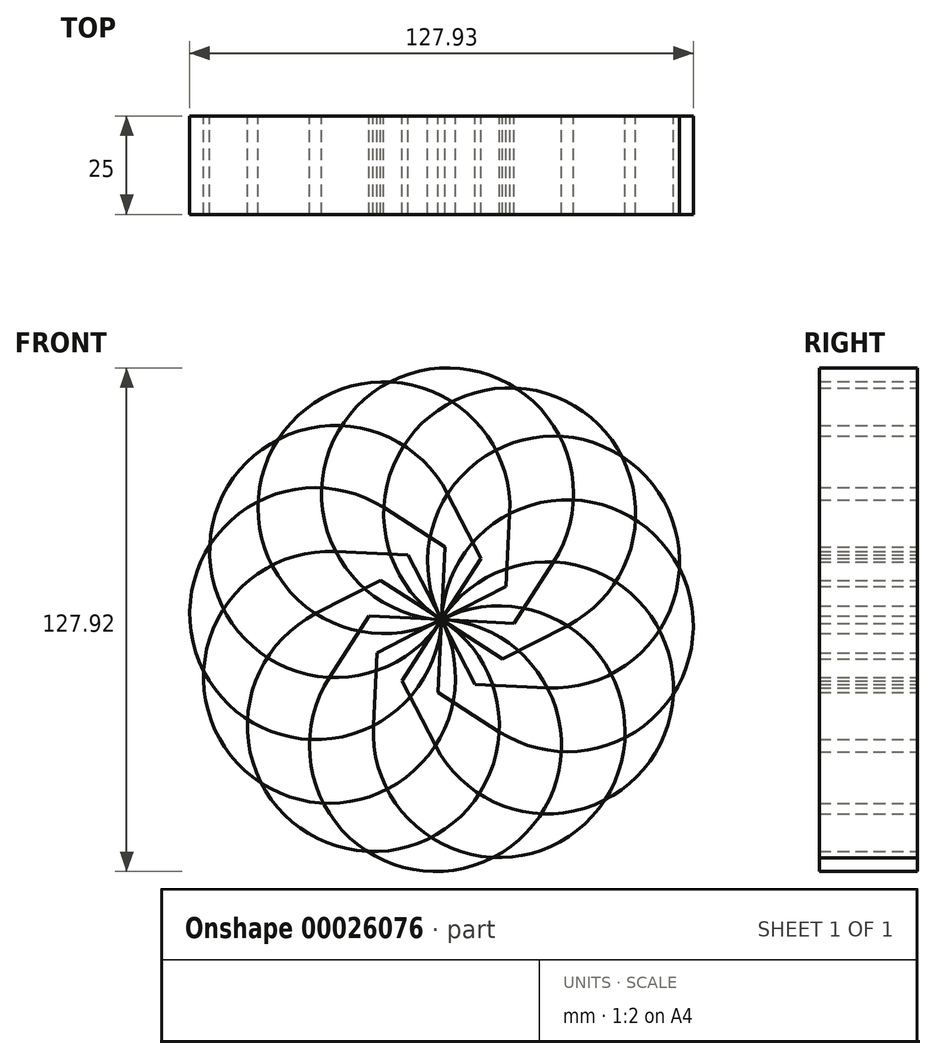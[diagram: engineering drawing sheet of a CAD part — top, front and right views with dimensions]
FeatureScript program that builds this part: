
annotation { "Feature Type Name" : "Feature", "Feature Type Description" : "" }
export const myFeature = defineFeature(function(context is Context, id is Id, definition is map)
    precondition{}
    {
        {
            var Q0;
            Q0=qCreatedBy(makeId("Front.planeOp"),FACE);
            var sketch = newSketch(context, id + "F0", { "sketchPlane" : qUnion([Q0])});
            skLineSegment(sketch, "E0.bottom", {"start": v(32.22, 19.52) * mm, "end": v(50.67, 18.63) * mm});
            skLineSegment(sketch, "E0.right", {"start": v(50.67, 18.63) * mm, "end": v(59.12, 2.2) * mm});
            skArc(sketch, "E1", {"start": v(32.22, 19.52) * mm, "mid": v(13.35, -39.35) * mm, "end": v(59.12, 2.2) * mm});
            skLineSegment(sketch, "E2.0", {"start": v(53.8, 23.48) * mm, "end": v(63, 5.6) * mm});
            skLineSegment(sketch, "E2.1", {"start": v(32.46, 24.52) * mm, "end": v(53.8, 23.48) * mm});
            skSolve(sketch);
        }
        {
            var Q0;
            Q0=makeQuery(id+"F0.imprint","IMPRINT",FACE,{"disambiguationData":[TD([[makeQuery(id+"F0.imprint","IMPRINT",EDGE,{"derivedFrom":sQuery(id+"F0.wireOp",EDGE,"E0.bottom")}),-1.0]])]});
            extrude(context, id + "F1", {"entities" : qUnion([Q0]), "endBound" : BoundingType.SYMMETRIC, "depth" : 25 * mm});
        }
        {
            var Q0;
            Q0=makeQuery(id+"F1.opExtrude","SWEPT_BODY",BODY,{"disambiguationData":[OSD([sQuery(id+"F0.wireOp",EDGE,"E0.bottom"),sQuery(id+"F0.wireOp",EDGE,"E0.right"),sQuery(id+"F0.wireOp",EDGE,"E1")])]});
            var Q1;
            Q1=makeQuery(id+"F1.opExtrude","SWEPT_EDGE",EDGE,{"disambiguationData":[OSD([sQuery(id+"F0.wireOp",EDGE,"E0.right"),sQuery(id+"F0.wireOp",EDGE,"E1")])]});
            circularPattern(context, id + "F2", {"entities" : qUnion([Q0]), "axis" : qUnion([Q1]), "angle" : 30 * degree, "instanceCount" : 50});
        }
    });
